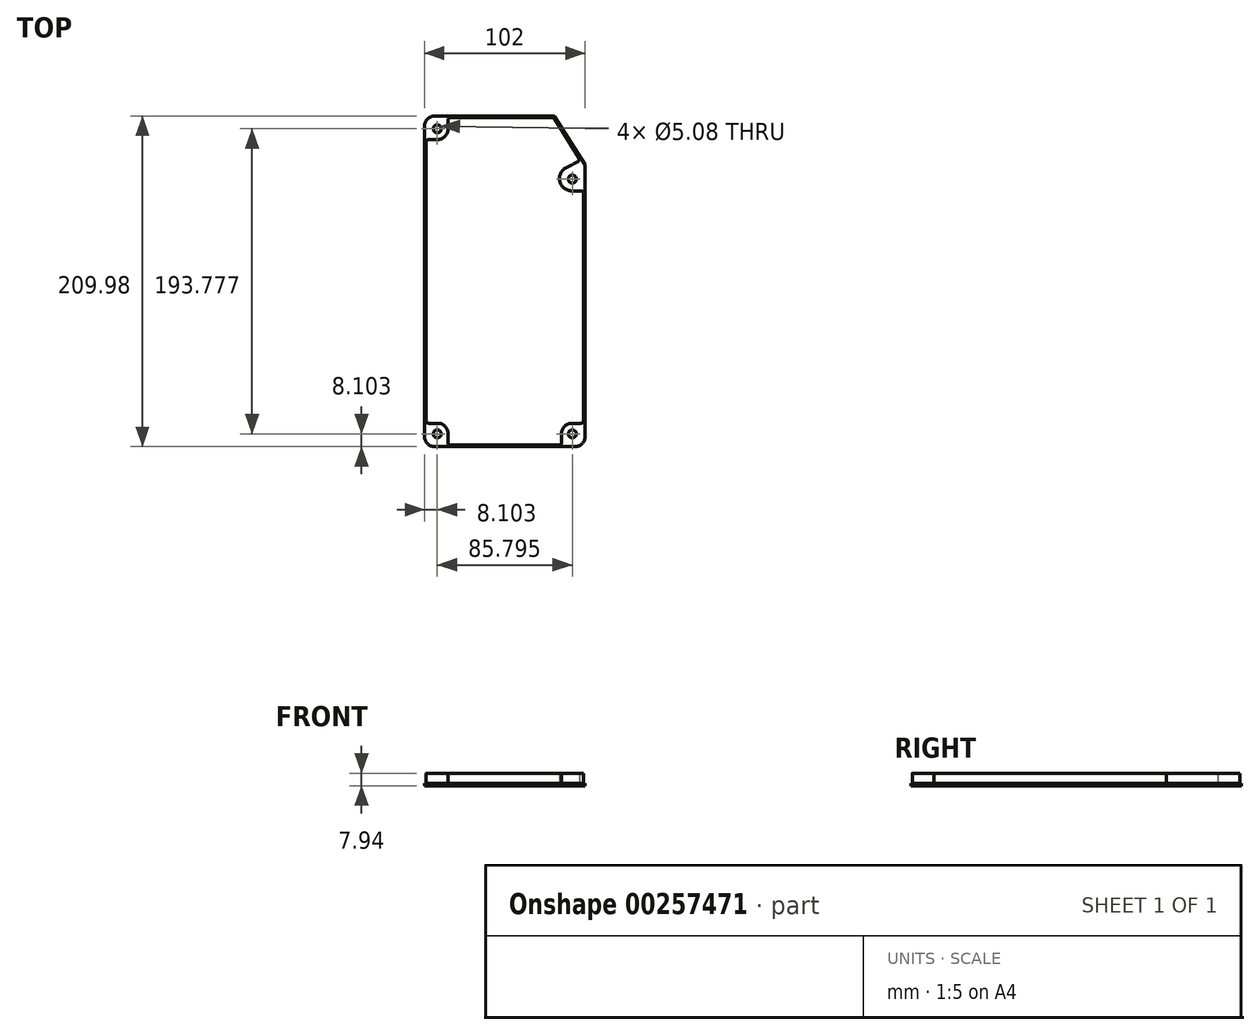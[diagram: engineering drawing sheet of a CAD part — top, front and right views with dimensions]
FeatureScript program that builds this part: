
annotation { "Feature Type Name" : "Feature", "Feature Type Description" : "" }
export const myFeature = defineFeature(function(context is Context, id is Id, definition is map)
    precondition{}
    {
        {
            var Q0;
            Q0=qCreatedBy(makeId("Top.planeOp"),FACE);
            var sketch = newSketch(context, id + "F0", { "sketchPlane" : qUnion([Q0])});
            skLineSegment(sketch, "E0.bottom", {"start": v(6.35, 0) * mm, "end": v(95.65, 0) * mm});
            skLineSegment(sketch, "E0.left", {"start": v(0, 6.35) * mm, "end": v(0, 203.63) * mm});
            skPoint(sketch, "E1.visualSharp", {"position": v(0, 209.98) * mm});
            skArc(sketch, "E1.filletArc", {"start": v(6.35, 209.98) * mm, "mid": v(1.86, 208.12) * mm, "end": v(0, 203.63) * mm});
            skPoint(sketch, "E2.visualSharp", {"position": v(102, 0) * mm});
            skArc(sketch, "E2.filletArc", {"start": v(95.65, 0) * mm, "mid": v(100.14, 1.86) * mm, "end": v(102, 6.35) * mm});
            skPoint(sketch, "E3.visualSharp", {"position": v(0, 0) * mm});
            skArc(sketch, "E3.filletArc", {"start": v(0, 6.35) * mm, "mid": v(1.86, 1.86) * mm, "end": v(6.35, 0) * mm});
            skCircle(sketch, "E4", {"center": v(8.1, 8.1) * mm, "radius": 2.54 * mm});
            skCircle(sketch, "E5", {"center": v(93.9, 8.1) * mm, "radius": 2.54 * mm});
            skCircle(sketch, "E6", {"center": v(8.1, 201.88) * mm, "radius": 2.54 * mm});
            skCircle(sketch, "E7", {"center": v(93.9, 169.93) * mm, "radius": 2.54 * mm});
            skLineSegment(sketch, "E8", {"start": v(82.7, 209.74) * mm, "end": v(101.92, 179.08) * mm});
            skLineSegment(sketch, "E9", {"start": v(6.35, 209.98) * mm, "end": v(82.27, 209.98) * mm});
            skLineSegment(sketch, "E10", {"start": v(102, 6.35) * mm, "end": v(102, 178.8) * mm});
            skPoint(sketch, "E11.visualSharp", {"position": v(82.55, 209.98) * mm});
            skArc(sketch, "E11.filletArc", {"start": v(82.7, 209.74) * mm, "mid": v(82.51, 209.92) * mm, "end": v(82.27, 209.98) * mm});
            skPoint(sketch, "E12.visualSharp", {"position": v(102, 178.95) * mm});
            skArc(sketch, "E12.filletArc", {"start": v(102, 178.8) * mm, "mid": v(101.98, 178.95) * mm, "end": v(101.92, 179.08) * mm});
            skSolve(sketch);
        }
        {
            var Q0;
            Q0 = qSketchRegion(id + "F0", true);
            extrude(context, id + "F1", {"entities" : qUnion([Q0]), "depth" : 1.59 * mm});
        }
        {
            var Q0;
            Q0=makeQuery(id+"F1.opExtrude","CAP_FACE",FACE,{"disambiguationData":[OSD([sQuery(id+"F0.wireOp",EDGE,"E0.bottom"),sQuery(id+"F0.wireOp",EDGE,"E0.top"),sQuery(id+"F0.wireOp",EDGE,"E0.left"),sQuery(id+"F0.wireOp",EDGE,"E0.right"),sQuery(id+"F0.wireOp",EDGE,"E1.filletArc"),sQuery(id+"F0.wireOp",EDGE,"4ccab8a7-fa3c-4ecf-96c5-f0e6e3bdf6ba.filletArc"),sQuery(id+"F0.wireOp",EDGE,"E2.filletArc"),sQuery(id+"F0.wireOp",EDGE,"E3.filletArc"),sQuery(id+"F0.wireOp",EDGE,"E4"),sQuery(id+"F0.wireOp",EDGE,"E5"),sQuery(id+"F0.wireOp",EDGE,"E6"),sQuery(id+"F0.wireOp",EDGE,"E7")])],"isStart":false});
            var sketch = newSketch(context, id + "F2", { "sketchPlane" : qUnion([Q0])});
            skLineSegment(sketch, "E13", {"start": v(16.45, 209) * mm, "end": v(81.11, 209) * mm});
            skLineSegment(sketch, "E14", {"start": v(82.46, 208.25) * mm, "end": v(98.07, 183.35) * mm});
            skLineSegment(sketch, "E15", {"start": v(93.62, 162.46) * mm, "end": v(99.33, 162.46) * mm});
            skLineSegment(sketch, "E16", {"start": v(100.91, 160.87) * mm, "end": v(100.91, 16.45) * mm});
            skLineSegment(sketch, "E17", {"start": v(99.33, 14.86) * mm, "end": v(93.5, 14.86) * mm});
            skLineSegment(sketch, "E18", {"start": v(87.14, 8.5) * mm, "end": v(87.14, 2.58) * mm});
            skLineSegment(sketch, "E19", {"start": v(85.55, 1) * mm, "end": v(16.45, 1) * mm});
            skLineSegment(sketch, "E20", {"start": v(14.86, 2.58) * mm, "end": v(14.86, 8.5) * mm});
            skLineSegment(sketch, "E21", {"start": v(8.5, 14.86) * mm, "end": v(2.58, 14.86) * mm});
            skLineSegment(sketch, "E22", {"start": v(1, 16.45) * mm, "end": v(1, 193.53) * mm});
            skLineSegment(sketch, "E23", {"start": v(2.58, 195.11) * mm, "end": v(8.5, 195.11) * mm});
            skLineSegment(sketch, "E24", {"start": v(14.86, 201.46) * mm, "end": v(14.86, 207.4) * mm});
            skPoint(sketch, "E25.visualSharp", {"position": v(14.86, 195.11) * mm});
            skArc(sketch, "E25.filletArc", {"start": v(8.5, 195.11) * mm, "mid": v(13, 196.97) * mm, "end": v(14.86, 201.46) * mm});
            skPoint(sketch, "E26.visualSharp", {"position": v(14.86, 14.86) * mm});
            skArc(sketch, "E26.filletArc", {"start": v(14.86, 8.5) * mm, "mid": v(13, 13) * mm, "end": v(8.5, 14.86) * mm});
            skPoint(sketch, "E27.visualSharp", {"position": v(87.14, 14.86) * mm});
            skArc(sketch, "E27.filletArc", {"start": v(93.5, 14.86) * mm, "mid": v(89, 13) * mm, "end": v(87.14, 8.5) * mm});
            skLineSegment(sketch, "E28", {"start": v(97.44, 181.09) * mm, "end": v(90.05, 177.32) * mm});
            skArc(sketch, "E29", {"start": v(90.05, 177.32) * mm, "mid": v(85.98, 168.48) * mm, "end": v(93.62, 162.46) * mm});
            skPoint(sketch, "E30.visualSharp", {"position": v(14.86, 209) * mm});
            skArc(sketch, "E30.filletArc", {"start": v(16.45, 209) * mm, "mid": v(15.32, 208.53) * mm, "end": v(14.86, 207.4) * mm});
            skPoint(sketch, "E31.visualSharp", {"position": v(82, 209) * mm});
            skArc(sketch, "E31.filletArc", {"start": v(82.46, 208.25) * mm, "mid": v(81.88, 208.8) * mm, "end": v(81.11, 209) * mm});
            skPoint(sketch, "E32.visualSharp", {"position": v(98.99, 181.88) * mm});
            skArc(sketch, "E32.filletArc", {"start": v(97.44, 181.09) * mm, "mid": v(98.25, 182.08) * mm, "end": v(98.07, 183.35) * mm});
            skPoint(sketch, "E33.visualSharp", {"position": v(100.91, 162.46) * mm});
            skArc(sketch, "E33.filletArc", {"start": v(100.91, 160.87) * mm, "mid": v(100.45, 162) * mm, "end": v(99.33, 162.46) * mm});
            skPoint(sketch, "E34.visualSharp", {"position": v(1, 195.11) * mm});
            skArc(sketch, "E34.filletArc", {"start": v(2.58, 195.11) * mm, "mid": v(1.46, 194.65) * mm, "end": v(1, 193.53) * mm});
            skPoint(sketch, "E35.visualSharp", {"position": v(1, 14.86) * mm});
            skArc(sketch, "E35.filletArc", {"start": v(1, 16.45) * mm, "mid": v(1.46, 15.32) * mm, "end": v(2.58, 14.86) * mm});
            skPoint(sketch, "E36.visualSharp", {"position": v(14.86, 1) * mm});
            skArc(sketch, "E36.filletArc", {"start": v(14.86, 2.58) * mm, "mid": v(15.32, 1.46) * mm, "end": v(16.45, 1) * mm});
            skPoint(sketch, "E37.visualSharp", {"position": v(87.14, 1) * mm});
            skArc(sketch, "E37.filletArc", {"start": v(85.55, 1) * mm, "mid": v(86.68, 1.46) * mm, "end": v(87.14, 2.58) * mm});
            skPoint(sketch, "E38.visualSharp", {"position": v(100.91, 14.86) * mm});
            skArc(sketch, "E38.filletArc", {"start": v(99.33, 14.86) * mm, "mid": v(100.45, 15.32) * mm, "end": v(100.91, 16.45) * mm});
            skSolve(sketch);
        }
        {
            var Q0;
            Q0 = qSketchRegion(id + "F2", true);
            extrude(context, id + "F3", {"entities" : qUnion([Q0]), "operationType" : NewBodyOperationType.ADD, "depth" : 6.35 * mm});
        }
    });
